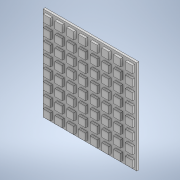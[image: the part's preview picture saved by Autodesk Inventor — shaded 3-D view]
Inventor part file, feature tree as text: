
AUTODESK INVENTOR PART (.ipt)
format: ipt  version: 2020.1 (Build 241239000, 239)  size: 395,776 bytes
history: native  units: in
note: dims shown in document units (in); Inventor stores cm internally (conversion verified against a paired STEP export)
features: extrude x2, sketch x2
ambient origin geometry x8: Origin, YZ Plane, XZ Plane, XY Plane, X Axis, Y Axis, Z Axis, Center Point
bodies: Solid1 (feature_tree)
feature tree (4):
  extrude  "Extrusion1"  Depth=2.5591in
  extrude  "Extrusion2"  Depth=0.0591in TaperAngle=0.0deg
  sketch  "Sketch2"  dims[d0=2.5591in d1=2.5591in]
  sketch  "Sketch3"  dims[d2=0.0591in d3=0.0in d65=0.0591in d66=0.0in]
